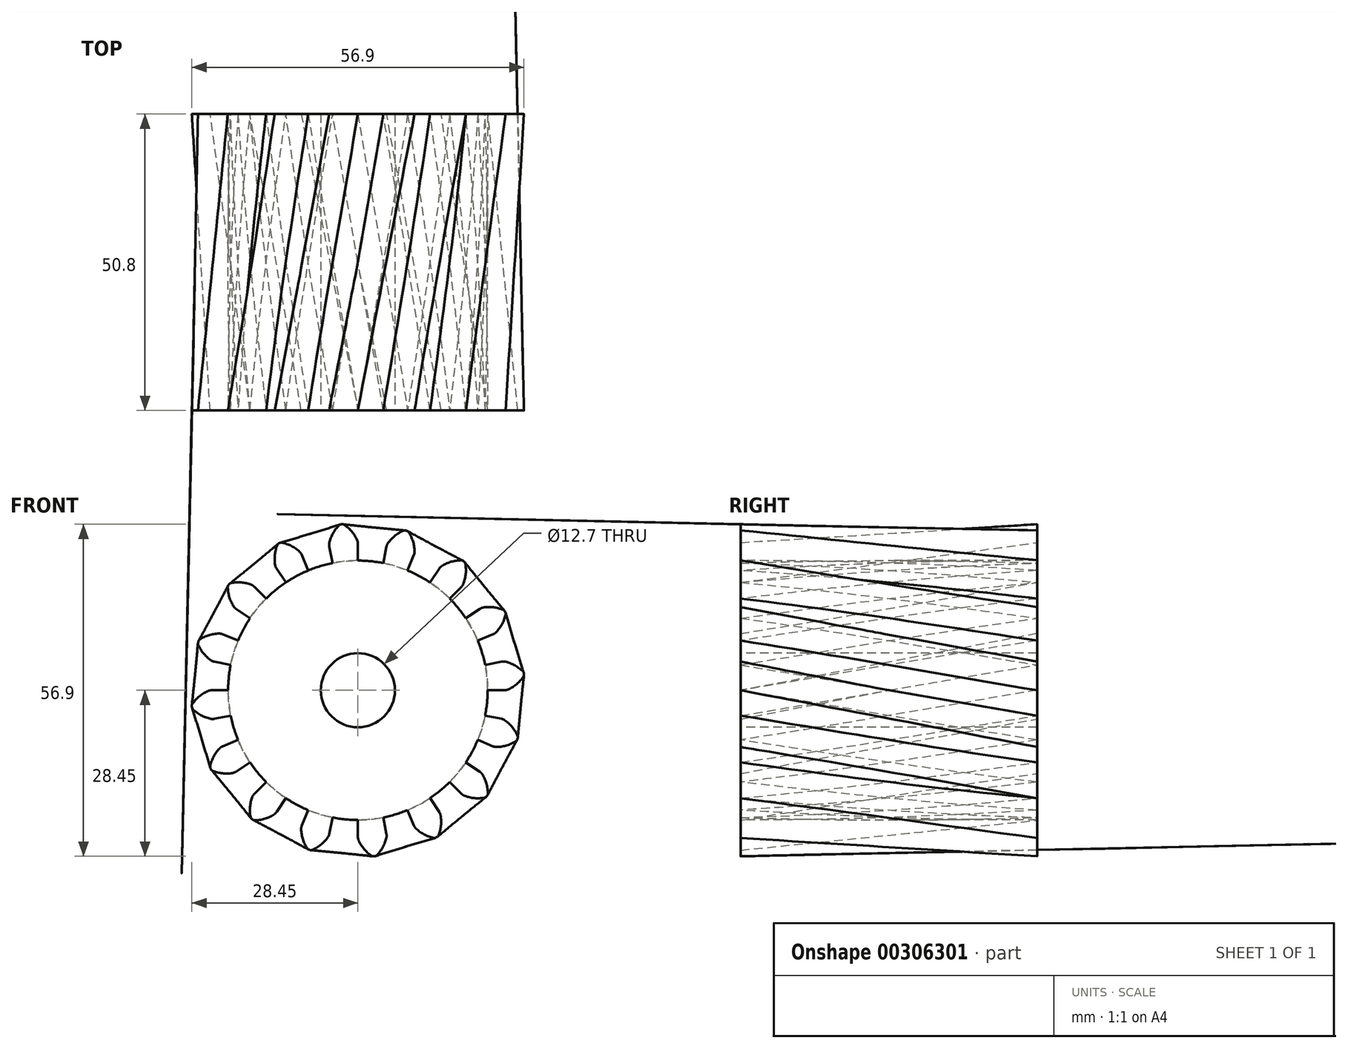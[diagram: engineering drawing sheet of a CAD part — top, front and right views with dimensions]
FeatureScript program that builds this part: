
annotation { "Feature Type Name" : "Feature", "Feature Type Description" : "" }
export const myFeature = defineFeature(function(context is Context, id is Id, definition is map)
    precondition{}
    {
        {
            var Q0;
            Q0=qCreatedBy(makeId("Front.planeOp"),FACE);
            var sketch = newSketch(context, id + "F0", { "sketchPlane" : qUnion([Q0])});
            skCircle(sketch, "E0", {"center": v(0, 0) * mm, "radius": 22.23 * mm});
            skArc(sketch, "E1.trimOffspring", {"start": v(-0.14, 25.74) * mm, "mid": v(-1.06, 27.2) * mm, "end": v(-2.34, 28.36) * mm});
            skLineSegment(sketch, "E2", {"start": v(0, 25.08) * mm, "end": v(0, 22.23) * mm});
            skLineSegment(sketch, "E3", {"start": v(-2.68, 28.45) * mm, "end": v(-2.8, 28.44) * mm});
            skLineSegment(sketch, "E4.MirrorCS", {"start": v(-4.9, 24.6) * mm, "end": v(-4.34, 21.8) * mm});
            skArc(sketch, "E5.MirrorCS", {"start": v(-4.88, 25.27) * mm, "mid": v(-4.27, 26.89) * mm, "end": v(-3.23, 28.28) * mm});
            skLineSegment(sketch, "E6.MirrorCS", {"start": v(-2.93, 28.43) * mm, "end": v(-2.8, 28.44) * mm});
            skPoint(sketch, "E7.visualSharp", {"position": v(-4.96, 24.91) * mm});
            skArc(sketch, "E7.filletArc", {"start": v(-4.88, 25.27) * mm, "mid": v(-4.92, 24.94) * mm, "end": v(-4.9, 24.6) * mm});
            skPoint(sketch, "E8.visualSharp", {"position": v(0, 25.4) * mm});
            skArc(sketch, "E8.filletArc", {"start": v(0, 25.08) * mm, "mid": v(-0.04, 25.42) * mm, "end": v(-0.14, 25.74) * mm});
            skPoint(sketch, "E9.visualSharp", {"position": v(-2.5, 28.47) * mm});
            skArc(sketch, "E9.filletArc", {"start": v(-2.34, 28.36) * mm, "mid": v(-2.5, 28.44) * mm, "end": v(-2.68, 28.45) * mm});
            skPoint(sketch, "E10.visualSharp", {"position": v(-3.1, 28.4) * mm});
            skArc(sketch, "E10.filletArc", {"start": v(-2.93, 28.43) * mm, "mid": v(-3.1, 28.38) * mm, "end": v(-3.23, 28.28) * mm});
            skSolve(sketch);
        }
        {
            var Q0;
            Q0=qCreatedBy(makeId("Front.planeOp"),FACE);
            cPlane(context, id + "F1", {"entities" : qUnion([Q0]), "cplaneType" : CPlaneType.OFFSET, "offset" : 50.8 * mm, "width" : 152.4 * mm, "height" : 152.4 * mm});
        }
        {
            var Q0;
            Q0=qCreatedBy(id+"F1.planeOp",FACE);
            var sketch = newSketch(context, id + "F2", { "sketchPlane" : qUnion([Q0])});
            skCircle(sketch, "E11.0", {"center": v(0, 0) * mm, "radius": 22.23 * mm});
            skArc(sketch, "E12.0.0", {"start": v(-3.23, 28.28) * mm, "mid": v(-4.27, 26.89) * mm, "end": v(-4.88, 25.27) * mm});
            skArc(sketch, "E12.0.1", {"start": v(-4.88, 25.27) * mm, "mid": v(-4.92, 24.94) * mm, "end": v(-4.9, 24.6) * mm});
            skLineSegment(sketch, "E12.0.2", {"start": v(-4.9, 24.6) * mm, "end": v(-4.34, 21.8) * mm});
            skArc(sketch, "E12.0.3", {"start": v(-4.34, 21.8) * mm, "mid": v(-2.18, 22.12) * mm, "end": v(0, 22.22) * mm});
            skLineSegment(sketch, "E12.0.4", {"start": v(0, 22.23) * mm, "end": v(0, 25.08) * mm});
            skArc(sketch, "E12.0.5", {"start": v(0, 25.08) * mm, "mid": v(-0.04, 25.42) * mm, "end": v(-0.14, 25.74) * mm});
            skArc(sketch, "E12.0.6", {"start": v(-0.14, 25.74) * mm, "mid": v(-1.06, 27.2) * mm, "end": v(-2.34, 28.36) * mm});
            skArc(sketch, "E12.0.7", {"start": v(-2.34, 28.36) * mm, "mid": v(-2.5, 28.44) * mm, "end": v(-2.68, 28.45) * mm});
            skLineSegment(sketch, "E12.0.8", {"start": v(-2.68, 28.45) * mm, "end": v(-2.8, 28.44) * mm});
            skLineSegment(sketch, "E12.0.9", {"start": v(-2.8, 28.44) * mm, "end": v(-2.93, 28.43) * mm});
            skArc(sketch, "E12.0.10", {"start": v(-2.93, 28.43) * mm, "mid": v(-3.1, 28.38) * mm, "end": v(-3.23, 28.28) * mm});
            skLineSegment(sketch, "E13.1.0", {"start": v(-13.94, 20.86) * mm, "end": v(-12.35, 18.48) * mm});
            skArc(sketch, "E13.1.1", {"start": v(-14.18, 21.48) * mm, "mid": v(-14.1, 21.15) * mm, "end": v(-13.94, 20.86) * mm});
            skArc(sketch, "E13.1.2", {"start": v(-13.8, 24.89) * mm, "mid": v(-14.23, 23.2) * mm, "end": v(-14.18, 21.48) * mm});
            skLineSegment(sketch, "E13.1.3", {"start": v(-8.5, 20.53) * mm, "end": v(-9.6, 23.17) * mm});
            skArc(sketch, "E13.1.4", {"start": v(-9.6, 23.17) * mm, "mid": v(-9.76, 23.47) * mm, "end": v(-9.98, 23.72) * mm});
            skArc(sketch, "E13.1.5", {"start": v(-9.98, 23.72) * mm, "mid": v(-11.4, 24.72) * mm, "end": v(-13.02, 25.3) * mm});
            skArc(sketch, "E13.1.6", {"start": v(-13.02, 25.3) * mm, "mid": v(-13.2, 25.31) * mm, "end": v(-13.36, 25.26) * mm});
            skArc(sketch, "E13.1.7", {"start": v(-13.58, 25.14) * mm, "mid": v(-13.72, 25.03) * mm, "end": v(-13.8, 24.89) * mm});
            skLineSegment(sketch, "E13.1.8", {"start": v(-13.47, 25.2) * mm, "end": v(-13.58, 25.14) * mm});
            skLineSegment(sketch, "E13.1.9", {"start": v(-13.36, 25.26) * mm, "end": v(-13.47, 25.2) * mm});
            skLineSegment(sketch, "E13.2.0", {"start": v(-20.86, 13.94) * mm, "end": v(-18.48, 12.35) * mm});
            skArc(sketch, "E13.2.1", {"start": v(-21.32, 14.42) * mm, "mid": v(-21.11, 14.15) * mm, "end": v(-20.86, 13.94) * mm});
            skArc(sketch, "E13.2.2", {"start": v(-22.28, 17.7) * mm, "mid": v(-22.03, 16) * mm, "end": v(-21.32, 14.42) * mm});
            skLineSegment(sketch, "E13.2.3", {"start": v(-15.72, 15.72) * mm, "end": v(-17.74, 17.74) * mm});
            skArc(sketch, "E13.2.4", {"start": v(-17.74, 17.74) * mm, "mid": v(-18, 17.95) * mm, "end": v(-18.3, 18.1) * mm});
            skArc(sketch, "E13.2.5", {"start": v(-18.3, 18.1) * mm, "mid": v(-19.99, 18.48) * mm, "end": v(-21.71, 18.4) * mm});
            skArc(sketch, "E13.2.6", {"start": v(-21.71, 18.4) * mm, "mid": v(-21.88, 18.34) * mm, "end": v(-22, 18.23) * mm});
            skArc(sketch, "E13.2.7", {"start": v(-22.17, 18.03) * mm, "mid": v(-22.25, 17.88) * mm, "end": v(-22.28, 17.7) * mm});
            skLineSegment(sketch, "E13.2.8", {"start": v(-22.1, 18.13) * mm, "end": v(-22.17, 18.03) * mm});
            skLineSegment(sketch, "E13.2.9", {"start": v(-22, 18.23) * mm, "end": v(-22.1, 18.13) * mm});
            skLineSegment(sketch, "E13.3.0", {"start": v(-24.6, 4.9) * mm, "end": v(-21.8, 4.34) * mm});
            skArc(sketch, "E13.3.1", {"start": v(-25.22, 5.16) * mm, "mid": v(-24.92, 5) * mm, "end": v(-24.6, 4.9) * mm});
            skArc(sketch, "E13.3.2", {"start": v(-27.36, 7.83) * mm, "mid": v(-26.47, 6.35) * mm, "end": v(-25.22, 5.16) * mm});
            skLineSegment(sketch, "E13.3.3", {"start": v(-20.53, 8.5) * mm, "end": v(-23.17, 9.6) * mm});
            skArc(sketch, "E13.3.4", {"start": v(-23.17, 9.6) * mm, "mid": v(-23.5, 9.7) * mm, "end": v(-23.83, 9.72) * mm});
            skArc(sketch, "E13.3.5", {"start": v(-23.83, 9.72) * mm, "mid": v(-25.54, 9.43) * mm, "end": v(-27.1, 8.69) * mm});
            skArc(sketch, "E13.3.6", {"start": v(-27.1, 8.69) * mm, "mid": v(-27.23, 8.57) * mm, "end": v(-27.3, 8.42) * mm});
            skArc(sketch, "E13.3.7", {"start": v(-27.38, 8.17) * mm, "mid": v(-27.4, 8) * mm, "end": v(-27.36, 7.83) * mm});
            skLineSegment(sketch, "E13.3.8", {"start": v(-27.35, 8.3) * mm, "end": v(-27.38, 8.17) * mm});
            skLineSegment(sketch, "E13.3.9", {"start": v(-27.3, 8.42) * mm, "end": v(-27.35, 8.3) * mm});
            skLineSegment(sketch, "E13.4.0", {"start": v(-24.6, -4.9) * mm, "end": v(-21.8, -4.34) * mm});
            skArc(sketch, "E13.4.1", {"start": v(-25.27, -4.88) * mm, "mid": v(-24.94, -4.92) * mm, "end": v(-24.6, -4.9) * mm});
            skArc(sketch, "E13.4.2", {"start": v(-28.28, -3.23) * mm, "mid": v(-26.89, -4.27) * mm, "end": v(-25.27, -4.88) * mm});
            skLineSegment(sketch, "E13.4.3", {"start": v(-22.23, 0) * mm, "end": v(-25.08, 0) * mm});
            skArc(sketch, "E13.4.4", {"start": v(-25.08, 0) * mm, "mid": v(-25.42, -0.04) * mm, "end": v(-25.74, -0.14) * mm});
            skArc(sketch, "E13.4.5", {"start": v(-25.74, -0.14) * mm, "mid": v(-27.2, -1.06) * mm, "end": v(-28.36, -2.34) * mm});
            skArc(sketch, "E13.4.6", {"start": v(-28.36, -2.34) * mm, "mid": v(-28.44, -2.5) * mm, "end": v(-28.45, -2.68) * mm});
            skArc(sketch, "E13.4.7", {"start": v(-28.43, -2.93) * mm, "mid": v(-28.38, -3.1) * mm, "end": v(-28.28, -3.23) * mm});
            skLineSegment(sketch, "E13.4.8", {"start": v(-28.44, -2.8) * mm, "end": v(-28.43, -2.93) * mm});
            skLineSegment(sketch, "E13.4.9", {"start": v(-28.45, -2.68) * mm, "end": v(-28.44, -2.8) * mm});
            skLineSegment(sketch, "E13.5.0", {"start": v(-20.86, -13.94) * mm, "end": v(-18.48, -12.35) * mm});
            skArc(sketch, "E13.5.1", {"start": v(-21.48, -14.18) * mm, "mid": v(-21.15, -14.1) * mm, "end": v(-20.86, -13.94) * mm});
            skArc(sketch, "E13.5.2", {"start": v(-24.89, -13.8) * mm, "mid": v(-23.2, -14.23) * mm, "end": v(-21.48, -14.18) * mm});
            skLineSegment(sketch, "E13.5.3", {"start": v(-20.53, -8.5) * mm, "end": v(-23.17, -9.6) * mm});
            skArc(sketch, "E13.5.4", {"start": v(-23.17, -9.6) * mm, "mid": v(-23.47, -9.76) * mm, "end": v(-23.72, -9.98) * mm});
            skArc(sketch, "E13.5.5", {"start": v(-23.72, -9.98) * mm, "mid": v(-24.72, -11.4) * mm, "end": v(-25.3, -13.02) * mm});
            skArc(sketch, "E13.5.6", {"start": v(-25.3, -13.02) * mm, "mid": v(-25.31, -13.2) * mm, "end": v(-25.26, -13.36) * mm});
            skArc(sketch, "E13.5.7", {"start": v(-25.14, -13.58) * mm, "mid": v(-25.03, -13.72) * mm, "end": v(-24.89, -13.8) * mm});
            skLineSegment(sketch, "E13.5.8", {"start": v(-25.2, -13.47) * mm, "end": v(-25.14, -13.58) * mm});
            skLineSegment(sketch, "E13.5.9", {"start": v(-25.26, -13.36) * mm, "end": v(-25.2, -13.47) * mm});
            skLineSegment(sketch, "E13.6.0", {"start": v(-13.94, -20.86) * mm, "end": v(-12.35, -18.48) * mm});
            skArc(sketch, "E13.6.1", {"start": v(-14.42, -21.32) * mm, "mid": v(-14.15, -21.11) * mm, "end": v(-13.94, -20.86) * mm});
            skArc(sketch, "E13.6.2", {"start": v(-17.7, -22.28) * mm, "mid": v(-16, -22.03) * mm, "end": v(-14.42, -21.32) * mm});
            skLineSegment(sketch, "E13.6.3", {"start": v(-15.72, -15.72) * mm, "end": v(-17.74, -17.74) * mm});
            skArc(sketch, "E13.6.4", {"start": v(-17.74, -17.74) * mm, "mid": v(-17.95, -18) * mm, "end": v(-18.1, -18.3) * mm});
            skArc(sketch, "E13.6.5", {"start": v(-18.1, -18.3) * mm, "mid": v(-18.48, -19.99) * mm, "end": v(-18.4, -21.71) * mm});
            skArc(sketch, "E13.6.6", {"start": v(-18.4, -21.71) * mm, "mid": v(-18.34, -21.88) * mm, "end": v(-18.23, -22) * mm});
            skArc(sketch, "E13.6.7", {"start": v(-18.03, -22.17) * mm, "mid": v(-17.88, -22.25) * mm, "end": v(-17.7, -22.28) * mm});
            skLineSegment(sketch, "E13.6.8", {"start": v(-18.13, -22.1) * mm, "end": v(-18.03, -22.17) * mm});
            skLineSegment(sketch, "E13.6.9", {"start": v(-18.23, -22) * mm, "end": v(-18.13, -22.1) * mm});
            skLineSegment(sketch, "E13.7.0", {"start": v(-4.9, -24.6) * mm, "end": v(-4.34, -21.8) * mm});
            skArc(sketch, "E13.7.1", {"start": v(-5.16, -25.22) * mm, "mid": v(-5, -24.92) * mm, "end": v(-4.9, -24.6) * mm});
            skArc(sketch, "E13.7.2", {"start": v(-7.83, -27.36) * mm, "mid": v(-6.35, -26.47) * mm, "end": v(-5.16, -25.22) * mm});
            skLineSegment(sketch, "E13.7.3", {"start": v(-8.5, -20.53) * mm, "end": v(-9.6, -23.17) * mm});
            skArc(sketch, "E13.7.4", {"start": v(-9.6, -23.17) * mm, "mid": v(-9.7, -23.5) * mm, "end": v(-9.72, -23.83) * mm});
            skArc(sketch, "E13.7.5", {"start": v(-9.72, -23.83) * mm, "mid": v(-9.43, -25.54) * mm, "end": v(-8.69, -27.1) * mm});
            skArc(sketch, "E13.7.6", {"start": v(-8.69, -27.1) * mm, "mid": v(-8.57, -27.23) * mm, "end": v(-8.42, -27.3) * mm});
            skArc(sketch, "E13.7.7", {"start": v(-8.17, -27.38) * mm, "mid": v(-8, -27.4) * mm, "end": v(-7.83, -27.36) * mm});
            skLineSegment(sketch, "E13.7.8", {"start": v(-8.3, -27.35) * mm, "end": v(-8.17, -27.38) * mm});
            skLineSegment(sketch, "E13.7.9", {"start": v(-8.42, -27.3) * mm, "end": v(-8.3, -27.35) * mm});
            skLineSegment(sketch, "E13.8.0", {"start": v(4.9, -24.6) * mm, "end": v(4.34, -21.8) * mm});
            skArc(sketch, "E13.8.1", {"start": v(4.88, -25.27) * mm, "mid": v(4.92, -24.94) * mm, "end": v(4.9, -24.6) * mm});
            skArc(sketch, "E13.8.2", {"start": v(3.23, -28.28) * mm, "mid": v(4.27, -26.89) * mm, "end": v(4.88, -25.27) * mm});
            skLineSegment(sketch, "E13.8.3", {"start": v(0, -22.23) * mm, "end": v(0, -25.08) * mm});
            skArc(sketch, "E13.8.4", {"start": v(0, -25.08) * mm, "mid": v(0.04, -25.42) * mm, "end": v(0.14, -25.74) * mm});
            skArc(sketch, "E13.8.5", {"start": v(0.14, -25.74) * mm, "mid": v(1.06, -27.2) * mm, "end": v(2.34, -28.36) * mm});
            skArc(sketch, "E13.8.6", {"start": v(2.34, -28.36) * mm, "mid": v(2.5, -28.44) * mm, "end": v(2.68, -28.45) * mm});
            skArc(sketch, "E13.8.7", {"start": v(2.93, -28.43) * mm, "mid": v(3.1, -28.38) * mm, "end": v(3.23, -28.28) * mm});
            skLineSegment(sketch, "E13.8.8", {"start": v(2.8, -28.44) * mm, "end": v(2.93, -28.43) * mm});
            skLineSegment(sketch, "E13.8.9", {"start": v(2.68, -28.45) * mm, "end": v(2.8, -28.44) * mm});
            skLineSegment(sketch, "E13.9.0", {"start": v(13.94, -20.86) * mm, "end": v(12.35, -18.48) * mm});
            skArc(sketch, "E13.9.1", {"start": v(14.18, -21.48) * mm, "mid": v(14.1, -21.15) * mm, "end": v(13.94, -20.86) * mm});
            skArc(sketch, "E13.9.2", {"start": v(13.8, -24.89) * mm, "mid": v(14.23, -23.2) * mm, "end": v(14.18, -21.48) * mm});
            skLineSegment(sketch, "E13.9.3", {"start": v(8.5, -20.53) * mm, "end": v(9.6, -23.17) * mm});
            skArc(sketch, "E13.9.4", {"start": v(9.6, -23.17) * mm, "mid": v(9.76, -23.47) * mm, "end": v(9.98, -23.72) * mm});
            skArc(sketch, "E13.9.5", {"start": v(9.98, -23.72) * mm, "mid": v(11.4, -24.72) * mm, "end": v(13.02, -25.3) * mm});
            skArc(sketch, "E13.9.6", {"start": v(13.02, -25.3) * mm, "mid": v(13.2, -25.31) * mm, "end": v(13.36, -25.26) * mm});
            skArc(sketch, "E13.9.7", {"start": v(13.58, -25.14) * mm, "mid": v(13.72, -25.03) * mm, "end": v(13.8, -24.89) * mm});
            skLineSegment(sketch, "E13.9.8", {"start": v(13.47, -25.2) * mm, "end": v(13.58, -25.14) * mm});
            skLineSegment(sketch, "E13.9.9", {"start": v(13.36, -25.26) * mm, "end": v(13.47, -25.2) * mm});
            skLineSegment(sketch, "E13.10.0", {"start": v(20.86, -13.94) * mm, "end": v(18.48, -12.35) * mm});
            skArc(sketch, "E13.10.1", {"start": v(21.32, -14.42) * mm, "mid": v(21.11, -14.15) * mm, "end": v(20.86, -13.94) * mm});
            skArc(sketch, "E13.10.2", {"start": v(22.28, -17.7) * mm, "mid": v(22.03, -16) * mm, "end": v(21.32, -14.42) * mm});
            skLineSegment(sketch, "E13.10.3", {"start": v(15.72, -15.72) * mm, "end": v(17.74, -17.74) * mm});
            skArc(sketch, "E13.10.4", {"start": v(17.74, -17.74) * mm, "mid": v(18, -17.95) * mm, "end": v(18.3, -18.1) * mm});
            skArc(sketch, "E13.10.5", {"start": v(18.3, -18.1) * mm, "mid": v(19.99, -18.48) * mm, "end": v(21.71, -18.4) * mm});
            skArc(sketch, "E13.10.6", {"start": v(21.71, -18.4) * mm, "mid": v(21.88, -18.34) * mm, "end": v(22, -18.23) * mm});
            skArc(sketch, "E13.10.7", {"start": v(22.17, -18.03) * mm, "mid": v(22.25, -17.88) * mm, "end": v(22.28, -17.7) * mm});
            skLineSegment(sketch, "E13.10.8", {"start": v(22.1, -18.13) * mm, "end": v(22.17, -18.03) * mm});
            skLineSegment(sketch, "E13.10.9", {"start": v(22, -18.23) * mm, "end": v(22.1, -18.13) * mm});
            skLineSegment(sketch, "E13.11.0", {"start": v(24.6, -4.9) * mm, "end": v(21.8, -4.34) * mm});
            skArc(sketch, "E13.11.1", {"start": v(25.22, -5.16) * mm, "mid": v(24.92, -5) * mm, "end": v(24.6, -4.9) * mm});
            skArc(sketch, "E13.11.2", {"start": v(27.36, -7.83) * mm, "mid": v(26.47, -6.35) * mm, "end": v(25.22, -5.16) * mm});
            skLineSegment(sketch, "E13.11.3", {"start": v(20.53, -8.5) * mm, "end": v(23.17, -9.6) * mm});
            skArc(sketch, "E13.11.4", {"start": v(23.17, -9.6) * mm, "mid": v(23.5, -9.7) * mm, "end": v(23.83, -9.72) * mm});
            skArc(sketch, "E13.11.5", {"start": v(23.83, -9.72) * mm, "mid": v(25.54, -9.43) * mm, "end": v(27.1, -8.69) * mm});
            skArc(sketch, "E13.11.6", {"start": v(27.1, -8.69) * mm, "mid": v(27.23, -8.57) * mm, "end": v(27.3, -8.42) * mm});
            skArc(sketch, "E13.11.7", {"start": v(27.38, -8.17) * mm, "mid": v(27.4, -8) * mm, "end": v(27.36, -7.83) * mm});
            skLineSegment(sketch, "E13.11.8", {"start": v(27.35, -8.3) * mm, "end": v(27.38, -8.17) * mm});
            skLineSegment(sketch, "E13.11.9", {"start": v(27.3, -8.42) * mm, "end": v(27.35, -8.3) * mm});
            skLineSegment(sketch, "E13.12.0", {"start": v(24.6, 4.9) * mm, "end": v(21.8, 4.34) * mm});
            skArc(sketch, "E13.12.1", {"start": v(25.27, 4.88) * mm, "mid": v(24.94, 4.92) * mm, "end": v(24.6, 4.9) * mm});
            skArc(sketch, "E13.12.2", {"start": v(28.28, 3.23) * mm, "mid": v(26.89, 4.27) * mm, "end": v(25.27, 4.88) * mm});
            skLineSegment(sketch, "E13.12.3", {"start": v(22.23, 0) * mm, "end": v(25.08, 0) * mm});
            skArc(sketch, "E13.12.4", {"start": v(25.08, 0) * mm, "mid": v(25.42, 0.04) * mm, "end": v(25.74, 0.14) * mm});
            skArc(sketch, "E13.12.5", {"start": v(25.74, 0.14) * mm, "mid": v(27.2, 1.06) * mm, "end": v(28.36, 2.34) * mm});
            skArc(sketch, "E13.12.6", {"start": v(28.36, 2.34) * mm, "mid": v(28.44, 2.5) * mm, "end": v(28.45, 2.68) * mm});
            skArc(sketch, "E13.12.7", {"start": v(28.43, 2.93) * mm, "mid": v(28.38, 3.1) * mm, "end": v(28.28, 3.23) * mm});
            skLineSegment(sketch, "E13.12.8", {"start": v(28.44, 2.8) * mm, "end": v(28.43, 2.93) * mm});
            skLineSegment(sketch, "E13.12.9", {"start": v(28.45, 2.68) * mm, "end": v(28.44, 2.8) * mm});
            skLineSegment(sketch, "E13.13.0", {"start": v(20.86, 13.94) * mm, "end": v(18.48, 12.35) * mm});
            skArc(sketch, "E13.13.1", {"start": v(21.48, 14.18) * mm, "mid": v(21.15, 14.1) * mm, "end": v(20.86, 13.94) * mm});
            skArc(sketch, "E13.13.2", {"start": v(24.89, 13.8) * mm, "mid": v(23.2, 14.23) * mm, "end": v(21.48, 14.18) * mm});
            skLineSegment(sketch, "E13.13.3", {"start": v(20.53, 8.5) * mm, "end": v(23.17, 9.6) * mm});
            skArc(sketch, "E13.13.4", {"start": v(23.17, 9.6) * mm, "mid": v(23.47, 9.76) * mm, "end": v(23.72, 9.98) * mm});
            skArc(sketch, "E13.13.5", {"start": v(23.72, 9.98) * mm, "mid": v(24.72, 11.4) * mm, "end": v(25.3, 13.02) * mm});
            skArc(sketch, "E13.13.6", {"start": v(25.3, 13.02) * mm, "mid": v(25.31, 13.2) * mm, "end": v(25.26, 13.36) * mm});
            skArc(sketch, "E13.13.7", {"start": v(25.14, 13.58) * mm, "mid": v(25.03, 13.72) * mm, "end": v(24.89, 13.8) * mm});
            skLineSegment(sketch, "E13.13.8", {"start": v(25.2, 13.47) * mm, "end": v(25.14, 13.58) * mm});
            skLineSegment(sketch, "E13.13.9", {"start": v(25.26, 13.36) * mm, "end": v(25.2, 13.47) * mm});
            skLineSegment(sketch, "E13.14.0", {"start": v(13.94, 20.86) * mm, "end": v(12.35, 18.48) * mm});
            skArc(sketch, "E13.14.1", {"start": v(14.42, 21.32) * mm, "mid": v(14.15, 21.11) * mm, "end": v(13.94, 20.86) * mm});
            skArc(sketch, "E13.14.2", {"start": v(17.7, 22.28) * mm, "mid": v(16, 22.03) * mm, "end": v(14.42, 21.32) * mm});
            skLineSegment(sketch, "E13.14.3", {"start": v(15.72, 15.72) * mm, "end": v(17.74, 17.74) * mm});
            skArc(sketch, "E13.14.4", {"start": v(17.74, 17.74) * mm, "mid": v(17.95, 18) * mm, "end": v(18.1, 18.3) * mm});
            skArc(sketch, "E13.14.5", {"start": v(18.1, 18.3) * mm, "mid": v(18.48, 19.99) * mm, "end": v(18.4, 21.71) * mm});
            skArc(sketch, "E13.14.6", {"start": v(18.4, 21.71) * mm, "mid": v(18.34, 21.88) * mm, "end": v(18.23, 22) * mm});
            skArc(sketch, "E13.14.7", {"start": v(18.03, 22.17) * mm, "mid": v(17.88, 22.25) * mm, "end": v(17.7, 22.28) * mm});
            skLineSegment(sketch, "E13.14.8", {"start": v(18.13, 22.1) * mm, "end": v(18.03, 22.17) * mm});
            skLineSegment(sketch, "E13.14.9", {"start": v(18.23, 22) * mm, "end": v(18.13, 22.1) * mm});
            skLineSegment(sketch, "E13.15.0", {"start": v(4.9, 24.6) * mm, "end": v(4.34, 21.8) * mm});
            skArc(sketch, "E13.15.1", {"start": v(5.16, 25.22) * mm, "mid": v(5, 24.92) * mm, "end": v(4.9, 24.6) * mm});
            skArc(sketch, "E13.15.2", {"start": v(7.83, 27.36) * mm, "mid": v(6.35, 26.47) * mm, "end": v(5.16, 25.22) * mm});
            skLineSegment(sketch, "E13.15.3", {"start": v(8.5, 20.53) * mm, "end": v(9.6, 23.17) * mm});
            skArc(sketch, "E13.15.4", {"start": v(9.6, 23.17) * mm, "mid": v(9.7, 23.5) * mm, "end": v(9.72, 23.83) * mm});
            skArc(sketch, "E13.15.5", {"start": v(9.72, 23.83) * mm, "mid": v(9.43, 25.54) * mm, "end": v(8.69, 27.1) * mm});
            skArc(sketch, "E13.15.6", {"start": v(8.69, 27.1) * mm, "mid": v(8.57, 27.23) * mm, "end": v(8.42, 27.3) * mm});
            skArc(sketch, "E13.15.7", {"start": v(8.17, 27.38) * mm, "mid": v(8, 27.4) * mm, "end": v(7.83, 27.36) * mm});
            skLineSegment(sketch, "E13.15.8", {"start": v(8.3, 27.35) * mm, "end": v(8.17, 27.38) * mm});
            skLineSegment(sketch, "E13.15.9", {"start": v(8.42, 27.3) * mm, "end": v(8.3, 27.35) * mm});
            skSolve(sketch);
        }
        {
            var Q0;
            Q0=makeQuery(id+"F0.imprint","IMPRINT",FACE,{"disambiguationData":[TD([[makeQuery(id+"F0.imprint","IMPRINT",EDGE,{"derivedFrom":sQuery(id+"F0.wireOp",EDGE,"E1.trimOffspring")}),1.0]])]});
            var Q1;
            {var subQ1=sQuery(id+"F2.wireOp",EDGE,"E13.1.0");Q1=makeQuery(id+"F2.imprint","IMPRINT",FACE,{"disambiguationData":[TD([[makeQuery(id+"F2.imprint","IMPRINT",EDGE,{"derivedFrom":subQ1}),1.0]])]});}
            loft(context, id + "F3", {"sheetProfilesArray" : [{ "sheetProfileEntities" : qUnion([Q0]) }, { "sheetProfileEntities" : qUnion([Q1]) }]});
        }
        {
            var Q0;
            Q0=qCreatedBy(id+"F1.planeOp",FACE);
            var sketch = newSketch(context, id + "F4", { "sketchPlane" : qUnion([Q0])});
            skCircle(sketch, "E14", {"center": v(0, 0) * mm, "radius": 22.22 * mm});
            skSolve(sketch);
        }
        {
            var Q0;
            Q0=makeQuery(id+"F4.imprint","IMPRINT",FACE,{"disambiguationData":[TD([[makeQuery(id+"F4.imprint","IMPRINT",EDGE,{"derivedFrom":sQuery(id+"F4.wireOp",EDGE,"E14")}),1.0]])]});
            extrude(context, id + "F5", {"entities" : qUnion([Q0]), "operationType" : NewBodyOperationType.ADD, "oppositeDirection" : true, "depth" : 50.8 * mm});
        }
        {
            var Q0;
            {var subQ1=sQuery(id+"F2.wireOp",EDGE,"E13.1.0");Q0=makeQuery(id+"F3.opLoft","SWEPT_BODY",BODY,{"disambiguationData":[OSD([makeQuery(id+"F0.imprint","IMPRINT",FACE,{"disambiguationData":[TD([[makeQuery(id+"F0.imprint","IMPRINT",EDGE,{"derivedFrom":sQuery(id+"F0.wireOp",EDGE,"E1.trimOffspring")}),1.0]])]}),makeQuery(id+"F2.imprint","IMPRINT",FACE,{"disambiguationData":[TD([[makeQuery(id+"F2.imprint","IMPRINT",EDGE,{"derivedFrom":subQ1}),1.0]])]})])]});}
            var Q1;
            Q1=makeQuery(id+"F5.opExtrude","SWEPT_FACE",FACE,{"disambiguationData":[OSD([sQuery(id+"F4.wireOp",EDGE,"E14")])]});
            circularPattern(context, id + "F6", {"entities" : qUnion([Q0]), "axis" : qUnion([Q1]), "angle" : 360 * degree, "instanceCount" : 16, "equalSpace" : true});
        }
        {
            var Q0;
            {var subQ1=sQuery(id+"F2.wireOp",EDGE,"E13.1.0");Q0=makeQuery(id+"F6.opPattern","COPY",BODY,{"derivedFrom":makeQuery(id+"F3.opLoft","SWEPT_BODY",BODY,{"disambiguationData":[OSD([makeQuery(id+"F0.imprint","IMPRINT",FACE,{"disambiguationData":[TD([[makeQuery(id+"F0.imprint","IMPRINT",EDGE,{"derivedFrom":sQuery(id+"F0.wireOp",EDGE,"E1.trimOffspring")}),1.0]])]}),makeQuery(id+"F2.imprint","IMPRINT",FACE,{"disambiguationData":[TD([[makeQuery(id+"F2.imprint","IMPRINT",EDGE,{"derivedFrom":subQ1}),1.0]])]})])]}),"instanceName":"8"});}
            var Q1;
            {var subQ1=sQuery(id+"F2.wireOp",EDGE,"E13.1.0");Q1=makeQuery(id+"F6.opPattern","COPY",BODY,{"derivedFrom":makeQuery(id+"F3.opLoft","SWEPT_BODY",BODY,{"disambiguationData":[OSD([makeQuery(id+"F0.imprint","IMPRINT",FACE,{"disambiguationData":[TD([[makeQuery(id+"F0.imprint","IMPRINT",EDGE,{"derivedFrom":sQuery(id+"F0.wireOp",EDGE,"E1.trimOffspring")}),1.0]])]}),makeQuery(id+"F2.imprint","IMPRINT",FACE,{"disambiguationData":[TD([[makeQuery(id+"F2.imprint","IMPRINT",EDGE,{"derivedFrom":subQ1}),1.0]])]})])]}),"instanceName":"9"});}
            var Q2;
            {var subQ1=sQuery(id+"F2.wireOp",EDGE,"E13.1.0");Q2=makeQuery(id+"F6.opPattern","COPY",BODY,{"derivedFrom":makeQuery(id+"F3.opLoft","SWEPT_BODY",BODY,{"disambiguationData":[OSD([makeQuery(id+"F0.imprint","IMPRINT",FACE,{"disambiguationData":[TD([[makeQuery(id+"F0.imprint","IMPRINT",EDGE,{"derivedFrom":sQuery(id+"F0.wireOp",EDGE,"E1.trimOffspring")}),1.0]])]}),makeQuery(id+"F2.imprint","IMPRINT",FACE,{"disambiguationData":[TD([[makeQuery(id+"F2.imprint","IMPRINT",EDGE,{"derivedFrom":subQ1}),1.0]])]})])]}),"instanceName":"10"});}
            var Q3;
            {var subQ1=sQuery(id+"F2.wireOp",EDGE,"E13.1.0");Q3=makeQuery(id+"F6.opPattern","COPY",BODY,{"derivedFrom":makeQuery(id+"F3.opLoft","SWEPT_BODY",BODY,{"disambiguationData":[OSD([makeQuery(id+"F0.imprint","IMPRINT",FACE,{"disambiguationData":[TD([[makeQuery(id+"F0.imprint","IMPRINT",EDGE,{"derivedFrom":sQuery(id+"F0.wireOp",EDGE,"E1.trimOffspring")}),1.0]])]}),makeQuery(id+"F2.imprint","IMPRINT",FACE,{"disambiguationData":[TD([[makeQuery(id+"F2.imprint","IMPRINT",EDGE,{"derivedFrom":subQ1}),1.0]])]})])]}),"instanceName":"11"});}
            var Q4;
            {var subQ1=sQuery(id+"F2.wireOp",EDGE,"E13.1.0");Q4=makeQuery(id+"F6.opPattern","COPY",BODY,{"derivedFrom":makeQuery(id+"F3.opLoft","SWEPT_BODY",BODY,{"disambiguationData":[OSD([makeQuery(id+"F0.imprint","IMPRINT",FACE,{"disambiguationData":[TD([[makeQuery(id+"F0.imprint","IMPRINT",EDGE,{"derivedFrom":sQuery(id+"F0.wireOp",EDGE,"E1.trimOffspring")}),1.0]])]}),makeQuery(id+"F2.imprint","IMPRINT",FACE,{"disambiguationData":[TD([[makeQuery(id+"F2.imprint","IMPRINT",EDGE,{"derivedFrom":subQ1}),1.0]])]})])]}),"instanceName":"12"});}
            var Q5;
            {var subQ1=sQuery(id+"F2.wireOp",EDGE,"E13.1.0");Q5=makeQuery(id+"F6.opPattern","COPY",BODY,{"derivedFrom":makeQuery(id+"F3.opLoft","SWEPT_BODY",BODY,{"disambiguationData":[OSD([makeQuery(id+"F0.imprint","IMPRINT",FACE,{"disambiguationData":[TD([[makeQuery(id+"F0.imprint","IMPRINT",EDGE,{"derivedFrom":sQuery(id+"F0.wireOp",EDGE,"E1.trimOffspring")}),1.0]])]}),makeQuery(id+"F2.imprint","IMPRINT",FACE,{"disambiguationData":[TD([[makeQuery(id+"F2.imprint","IMPRINT",EDGE,{"derivedFrom":subQ1}),1.0]])]})])]}),"instanceName":"13"});}
            var Q6;
            {var subQ1=sQuery(id+"F2.wireOp",EDGE,"E13.1.0");Q6=makeQuery(id+"F6.opPattern","COPY",BODY,{"derivedFrom":makeQuery(id+"F3.opLoft","SWEPT_BODY",BODY,{"disambiguationData":[OSD([makeQuery(id+"F0.imprint","IMPRINT",FACE,{"disambiguationData":[TD([[makeQuery(id+"F0.imprint","IMPRINT",EDGE,{"derivedFrom":sQuery(id+"F0.wireOp",EDGE,"E1.trimOffspring")}),1.0]])]}),makeQuery(id+"F2.imprint","IMPRINT",FACE,{"disambiguationData":[TD([[makeQuery(id+"F2.imprint","IMPRINT",EDGE,{"derivedFrom":subQ1}),1.0]])]})])]}),"instanceName":"14"});}
            var Q7;
            {var subQ1=sQuery(id+"F2.wireOp",EDGE,"E13.1.0");Q7=makeQuery(id+"F6.opPattern","COPY",BODY,{"derivedFrom":makeQuery(id+"F3.opLoft","SWEPT_BODY",BODY,{"disambiguationData":[OSD([makeQuery(id+"F0.imprint","IMPRINT",FACE,{"disambiguationData":[TD([[makeQuery(id+"F0.imprint","IMPRINT",EDGE,{"derivedFrom":sQuery(id+"F0.wireOp",EDGE,"E1.trimOffspring")}),1.0]])]}),makeQuery(id+"F2.imprint","IMPRINT",FACE,{"disambiguationData":[TD([[makeQuery(id+"F2.imprint","IMPRINT",EDGE,{"derivedFrom":subQ1}),1.0]])]})])]}),"instanceName":"15"});}
            var Q8;
            {var subQ1=sQuery(id+"F2.wireOp",EDGE,"E13.1.0");Q8=makeQuery(id+"F3.opLoft","SWEPT_BODY",BODY,{"disambiguationData":[OSD([makeQuery(id+"F0.imprint","IMPRINT",FACE,{"disambiguationData":[TD([[makeQuery(id+"F0.imprint","IMPRINT",EDGE,{"derivedFrom":sQuery(id+"F0.wireOp",EDGE,"E1.trimOffspring")}),1.0]])]}),makeQuery(id+"F2.imprint","IMPRINT",FACE,{"disambiguationData":[TD([[makeQuery(id+"F2.imprint","IMPRINT",EDGE,{"derivedFrom":subQ1}),1.0]])]})])]});}
            var Q9;
            {var subQ1=sQuery(id+"F2.wireOp",EDGE,"E13.1.0");Q9=makeQuery(id+"F6.opPattern","COPY",BODY,{"derivedFrom":makeQuery(id+"F3.opLoft","SWEPT_BODY",BODY,{"disambiguationData":[OSD([makeQuery(id+"F0.imprint","IMPRINT",FACE,{"disambiguationData":[TD([[makeQuery(id+"F0.imprint","IMPRINT",EDGE,{"derivedFrom":sQuery(id+"F0.wireOp",EDGE,"E1.trimOffspring")}),1.0]])]}),makeQuery(id+"F2.imprint","IMPRINT",FACE,{"disambiguationData":[TD([[makeQuery(id+"F2.imprint","IMPRINT",EDGE,{"derivedFrom":subQ1}),1.0]])]})])]}),"instanceName":"1"});}
            var Q10;
            {var subQ1=sQuery(id+"F2.wireOp",EDGE,"E13.1.0");Q10=makeQuery(id+"F6.opPattern","COPY",BODY,{"derivedFrom":makeQuery(id+"F3.opLoft","SWEPT_BODY",BODY,{"disambiguationData":[OSD([makeQuery(id+"F0.imprint","IMPRINT",FACE,{"disambiguationData":[TD([[makeQuery(id+"F0.imprint","IMPRINT",EDGE,{"derivedFrom":sQuery(id+"F0.wireOp",EDGE,"E1.trimOffspring")}),1.0]])]}),makeQuery(id+"F2.imprint","IMPRINT",FACE,{"disambiguationData":[TD([[makeQuery(id+"F2.imprint","IMPRINT",EDGE,{"derivedFrom":subQ1}),1.0]])]})])]}),"instanceName":"2"});}
            var Q11;
            {var subQ1=sQuery(id+"F2.wireOp",EDGE,"E13.1.0");Q11=makeQuery(id+"F6.opPattern","COPY",BODY,{"derivedFrom":makeQuery(id+"F3.opLoft","SWEPT_BODY",BODY,{"disambiguationData":[OSD([makeQuery(id+"F0.imprint","IMPRINT",FACE,{"disambiguationData":[TD([[makeQuery(id+"F0.imprint","IMPRINT",EDGE,{"derivedFrom":sQuery(id+"F0.wireOp",EDGE,"E1.trimOffspring")}),1.0]])]}),makeQuery(id+"F2.imprint","IMPRINT",FACE,{"disambiguationData":[TD([[makeQuery(id+"F2.imprint","IMPRINT",EDGE,{"derivedFrom":subQ1}),1.0]])]})])]}),"instanceName":"3"});}
            var Q12;
            {var subQ1=sQuery(id+"F2.wireOp",EDGE,"E13.1.0");Q12=makeQuery(id+"F6.opPattern","COPY",BODY,{"derivedFrom":makeQuery(id+"F3.opLoft","SWEPT_BODY",BODY,{"disambiguationData":[OSD([makeQuery(id+"F0.imprint","IMPRINT",FACE,{"disambiguationData":[TD([[makeQuery(id+"F0.imprint","IMPRINT",EDGE,{"derivedFrom":sQuery(id+"F0.wireOp",EDGE,"E1.trimOffspring")}),1.0]])]}),makeQuery(id+"F2.imprint","IMPRINT",FACE,{"disambiguationData":[TD([[makeQuery(id+"F2.imprint","IMPRINT",EDGE,{"derivedFrom":subQ1}),1.0]])]})])]}),"instanceName":"4"});}
            var Q13;
            {var subQ1=sQuery(id+"F2.wireOp",EDGE,"E13.1.0");Q13=makeQuery(id+"F6.opPattern","COPY",BODY,{"derivedFrom":makeQuery(id+"F3.opLoft","SWEPT_BODY",BODY,{"disambiguationData":[OSD([makeQuery(id+"F0.imprint","IMPRINT",FACE,{"disambiguationData":[TD([[makeQuery(id+"F0.imprint","IMPRINT",EDGE,{"derivedFrom":sQuery(id+"F0.wireOp",EDGE,"E1.trimOffspring")}),1.0]])]}),makeQuery(id+"F2.imprint","IMPRINT",FACE,{"disambiguationData":[TD([[makeQuery(id+"F2.imprint","IMPRINT",EDGE,{"derivedFrom":subQ1}),1.0]])]})])]}),"instanceName":"5"});}
            var Q14;
            {var subQ1=sQuery(id+"F2.wireOp",EDGE,"E13.1.0");Q14=makeQuery(id+"F6.opPattern","COPY",BODY,{"derivedFrom":makeQuery(id+"F3.opLoft","SWEPT_BODY",BODY,{"disambiguationData":[OSD([makeQuery(id+"F0.imprint","IMPRINT",FACE,{"disambiguationData":[TD([[makeQuery(id+"F0.imprint","IMPRINT",EDGE,{"derivedFrom":sQuery(id+"F0.wireOp",EDGE,"E1.trimOffspring")}),1.0]])]}),makeQuery(id+"F2.imprint","IMPRINT",FACE,{"disambiguationData":[TD([[makeQuery(id+"F2.imprint","IMPRINT",EDGE,{"derivedFrom":subQ1}),1.0]])]})])]}),"instanceName":"6"});}
            var Q15;
            {var subQ1=sQuery(id+"F2.wireOp",EDGE,"E13.1.0");Q15=makeQuery(id+"F6.opPattern","COPY",BODY,{"derivedFrom":makeQuery(id+"F3.opLoft","SWEPT_BODY",BODY,{"disambiguationData":[OSD([makeQuery(id+"F0.imprint","IMPRINT",FACE,{"disambiguationData":[TD([[makeQuery(id+"F0.imprint","IMPRINT",EDGE,{"derivedFrom":sQuery(id+"F0.wireOp",EDGE,"E1.trimOffspring")}),1.0]])]}),makeQuery(id+"F2.imprint","IMPRINT",FACE,{"disambiguationData":[TD([[makeQuery(id+"F2.imprint","IMPRINT",EDGE,{"derivedFrom":subQ1}),1.0]])]})])]}),"instanceName":"7"});}
            booleanBodies(context, id + "F7", {"operationType" : BooleanOperationType.UNION, "tools" : qUnion([Q0, Q1, Q2, Q3, Q4, Q5, Q6, Q7, Q8, Q9, Q10, Q11, Q12, Q13, Q14, Q15])});
        }
        {
            var Q0;
            {var subQ1=sQuery(id+"F2.wireOp",EDGE,"E13.1.0");var subQ3=makeQuery(id+"F5.boolean.opBoolean","MERGE",FACE,{"derivedFrom":[makeQuery(id+"F3.opLoft","CAP_FACE",FACE,{"disambiguationData":[OSD([makeQuery(id+"F2.imprint","IMPRINT",FACE,{"disambiguationData":[TD([[makeQuery(id+"F2.imprint","IMPRINT",EDGE,{"derivedFrom":subQ1}),1.0]])]})])],"isStart":true}),makeQuery(id+"F5.opExtrude","CAP_FACE",FACE,{"disambiguationData":[OSD([sQuery(id+"F4.wireOp",EDGE,"E14")])],"isStart":true})]});Q0=makeQuery(id+"F7.opBoolean","MERGE",FACE,{"derivedFrom":[subQ3,makeQuery(id+"F6.opPattern","COPY",FACE,{"derivedFrom":subQ3,"instanceName":"1"}),makeQuery(id+"F6.opPattern","COPY",FACE,{"derivedFrom":subQ3,"instanceName":"2"}),makeQuery(id+"F6.opPattern","COPY",FACE,{"derivedFrom":subQ3,"instanceName":"3"}),makeQuery(id+"F6.opPattern","COPY",FACE,{"derivedFrom":subQ3,"instanceName":"4"}),makeQuery(id+"F6.opPattern","COPY",FACE,{"derivedFrom":subQ3,"instanceName":"5"}),makeQuery(id+"F6.opPattern","COPY",FACE,{"derivedFrom":subQ3,"instanceName":"6"}),makeQuery(id+"F6.opPattern","COPY",FACE,{"derivedFrom":subQ3,"instanceName":"7"}),makeQuery(id+"F6.opPattern","COPY",FACE,{"derivedFrom":subQ3,"instanceName":"8"}),makeQuery(id+"F6.opPattern","COPY",FACE,{"derivedFrom":subQ3,"instanceName":"9"}),makeQuery(id+"F6.opPattern","COPY",FACE,{"derivedFrom":subQ3,"instanceName":"10"}),makeQuery(id+"F6.opPattern","COPY",FACE,{"derivedFrom":subQ3,"instanceName":"11"}),makeQuery(id+"F6.opPattern","COPY",FACE,{"derivedFrom":subQ3,"instanceName":"12"}),makeQuery(id+"F6.opPattern","COPY",FACE,{"derivedFrom":subQ3,"instanceName":"13"}),makeQuery(id+"F6.opPattern","COPY",FACE,{"derivedFrom":subQ3,"instanceName":"14"}),makeQuery(id+"F6.opPattern","COPY",FACE,{"derivedFrom":subQ3,"instanceName":"15"})]});}
            var sketch = newSketch(context, id + "F8", { "sketchPlane" : qUnion([Q0])});
            skPoint(sketch, "E15", {"position": v(0, 0) * mm});
            skSolve(sketch);
        }
        {
            var Q0;
            Q0=sQuery(id+"F8.wireOp",VERTEX,"E15");
            var Q1;
            {var subQ1=sQuery(id+"F2.wireOp",EDGE,"E13.1.0");Q1=makeQuery(id+"F6.opPattern","COPY",BODY,{"derivedFrom":makeQuery(id+"F3.opLoft","SWEPT_BODY",BODY,{"disambiguationData":[OSD([makeQuery(id+"F0.imprint","IMPRINT",FACE,{"disambiguationData":[TD([[makeQuery(id+"F0.imprint","IMPRINT",EDGE,{"derivedFrom":sQuery(id+"F0.wireOp",EDGE,"E1.trimOffspring")}),1.0]])]}),makeQuery(id+"F2.imprint","IMPRINT",FACE,{"disambiguationData":[TD([[makeQuery(id+"F2.imprint","IMPRINT",EDGE,{"derivedFrom":subQ1}),1.0]])]})])]}),"instanceName":"8"});}
            hole(context, id + "F9", {"style" : HoleStyle.SIMPLE, "endStyle" : HoleEndStyle.THROUGH, "holeDiameter" : 12.7 * mm, "tappedDepth" : 12.7 * mm, "tapClearance" : 3, "locations" : qUnion([Q0]), "scope" : qUnion([Q1])});
        }
    });
